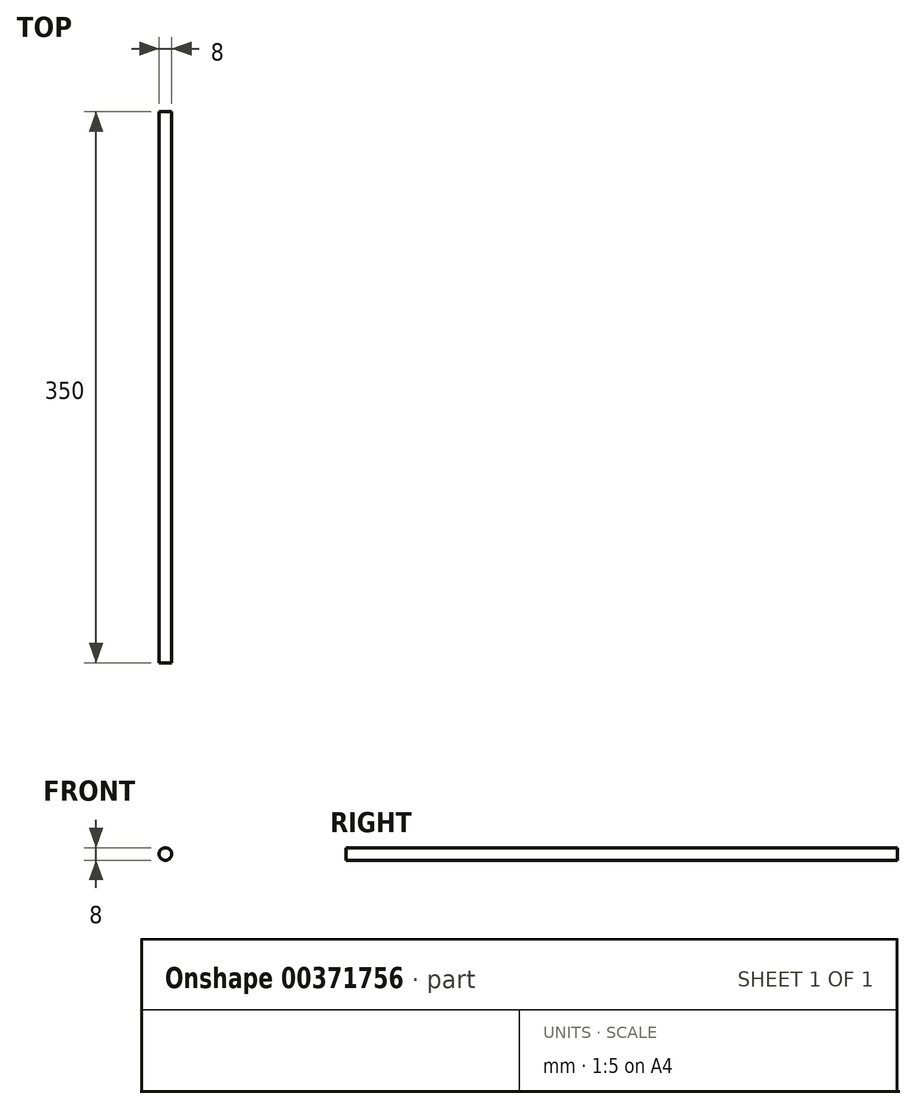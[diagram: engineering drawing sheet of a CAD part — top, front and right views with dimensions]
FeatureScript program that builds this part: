
annotation { "Feature Type Name" : "Feature", "Feature Type Description" : "" }
export const myFeature = defineFeature(function(context is Context, id is Id, definition is map)
    precondition{}
    {
        {
            var Q0;
            Q0=qCreatedBy(makeId("Front.planeOp"),FACE);
            var sketch = newSketch(context, id + "F0", { "sketchPlane" : qUnion([Q0])});
            skCircle(sketch, "E0", {"center": v(0, 0) * mm, "radius": 4 * mm});
            skSolve(sketch);
        }
        {
            assignVariable(context, id + "F1", {"name" : "x", "anyValue" : 350});
        }
        {
            var Q0;
            Q0=makeQuery(id+"F0.imprint","IMPRINT",FACE,{"disambiguationData":[TD([[makeQuery(id+"F0.imprint","IMPRINT",EDGE,{"derivedFrom":sQuery(id+"F0.wireOp",EDGE,"E0")}),1.0]])]});
            extrude(context, id + "F2", {"entities" : qUnion([Q0]), "depth" : (getVariable(context, 'x')) * mm});
        }
    });
